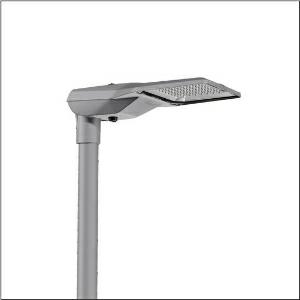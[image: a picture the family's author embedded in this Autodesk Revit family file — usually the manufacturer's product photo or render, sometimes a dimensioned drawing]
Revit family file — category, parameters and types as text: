
# Revit family: streetlight_sl_21_midi___st1_0a_5xe3d33t08lb_3fd1
name_source: partatom
category: Lighting Fixtures
units: mm (PartAtom-declared; Revit-internal decimal feet)

## family parameters
Cut with Voids When Loaded = No
Host = Face
Light Source = No
Part Type = Normal
Room Calculation Point = No
Round Connector Dimension = Use Diameter
Shared = No

## types (1)
- --- (1 x LED, 14340 lm, 99.6 W, 3000K)
    Apparent Load = 100 VA
    CIE Flux Codes = 37 72 97 100 100
    Color Rendering = 70
    Color Temperature = 3000K
    Default Elevation = 1800 mm
    Description = Streetlight SL 21 midi, mast luminaire, primary light control with lens, of PMMA, primary optical cover: cover, of toughened safety glass, transparent, light distribution: ST1.0a, light emission: direct distribution, primary light characteristic: asymmetric, installation type: side-entry, post-top, LED, High Power LED, rated luminous flux: 14.340lm, luminous efficacy: 144lm/W, light colour: 730, colour temperature: 3000K, control gear: D4i, control: flexible luminous flux parameterisation, time-dependent luminous flux control, constant luminous flux control, overheat protection, pre-setting: logarithmic dimming characteristic, mains connection: 230..240V, AC, 50/60Hz, start of lifetime: 100W, end of service life: 102W, reduction: 46W, luminaire housing, of diecast aluminium, powder-coated, Siteco® metallic grey (DB 702S), corrosivity category C5 mid according to DIN EN ISO 12944, please order mast flange separately, inclination adjustable: 0°, 5°, 10°, 15°, sealing non-destructively replaceable, multi-level sealing system, length: 644mm, width: 335mm, height: 110mm, mast flange for spigot size: 42mm (side-entry): 5XC10008XM4, 60/48mm (side-entry/post-top): 5XC10108XM2, 76/60mm (side-entry/post-top): 5XC10108XM1, mounting height: 4..8m, Smart Interface below and above, protection rating (complete): IP66, insulation class (complete): insulation class II (safety insulation), certification: CE, ENEC, ENEC+, VDE, impact resistance: IK10, permissible operating ambient temperature for outdoor applications: -40..+50°C, standard-compliant lighting for roads and squares, packaging unit: 1 piece

Light Distribution: ST1.0a
    Height = 111 mm
    Lamp = 1 x LED
    Lamp Light Flux = 14340 lm
    Lamp Power = 99.6 W
    Lamp count = 1
    Length = 644 mm
    Luminous efficacy = 144 lm/W
    Manufacturer = Siteco
    ModVariant = No
    Model = 5XE3D33T08LB
    Number of Poles = 1
    OnlyDefault = Yes
    Power Factor = 1
    Product Name = Streetlight SL 21 midi | ST1.0a
    Product group = mast luminaire | pylon top
    ProductGroupID = 6100
    Protection Class = Protection class II
    Protection Degree = IP 66
    RLX_Detail_Level = 1
    RLX_Emergency_Light_Flux = 0 lm
    RLX_Emergency_Type = 0
    RLX_Emergency_Type_DB = No
    RlxData = <blob elided: 26929 chars, md5=07e7fc97>
    Socket = socket
    Standby Power = 0 W
    System Light Flux = 14340 lm
    System Power = 100 W
    Type Comments = factory setting: luminous flux: 100 % | dim-lin: 254 | 1020 mA
    Type Image = l_1004304.jpg
    URL = http://relux.com
    VarID = @adj_031895
    Voltage = 0 V
    Weight = 0.00 kg
    Width = 336 mm

## geometry (parser evidence)
native form markers: Blend x4, Sweep x10
no freeform markers — native parametric forms only
